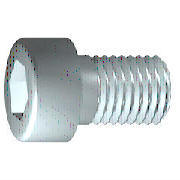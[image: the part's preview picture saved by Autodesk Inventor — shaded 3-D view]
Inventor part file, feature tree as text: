
AUTODESK INVENTOR PART (.ipt)
format: ipt  version: 2011 (Build 150239000, 239)  size: 181,760 bytes
history: native  units: mm (DEFAULTED — no unit token found)
features: extrude x1, plane x1
ambient origin geometry x7: Origin, YZ Plane, XY Plane, X Axis, Y Axis, Z Axis, Center Point
bodies: Solid1 (feature_tree), Body (feature_tree)
feature tree (2):
  extrude  "Slot"  Depth=31.75mm
  plane  "Work Plane1"
